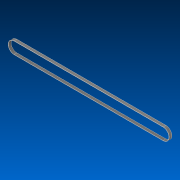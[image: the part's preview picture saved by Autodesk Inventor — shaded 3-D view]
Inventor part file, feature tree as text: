
AUTODESK INVENTOR PART (.ipt)
format: ipt  version: 2022 (Build 260153000, 153)  size: 90,624 bytes
history: native  units: in
note: dims shown in document units (in); Inventor stores cm internally (conversion verified against a paired STEP export)
features: extrude x1, sketch x1
ambient origin geometry x8: Origin, YZ Plane, XZ Plane, XY Plane, X Axis, Y Axis, Z Axis, Center Point
bodies: Solid1 (feature_tree)
feature tree (2):
  extrude  "Extrusion1"  Depth=1.504in
  sketch  "Sketch1"  dims[d0=19.5in d1=1.504in d2=0.0394in d3=0.3543in d4=0.0in]
